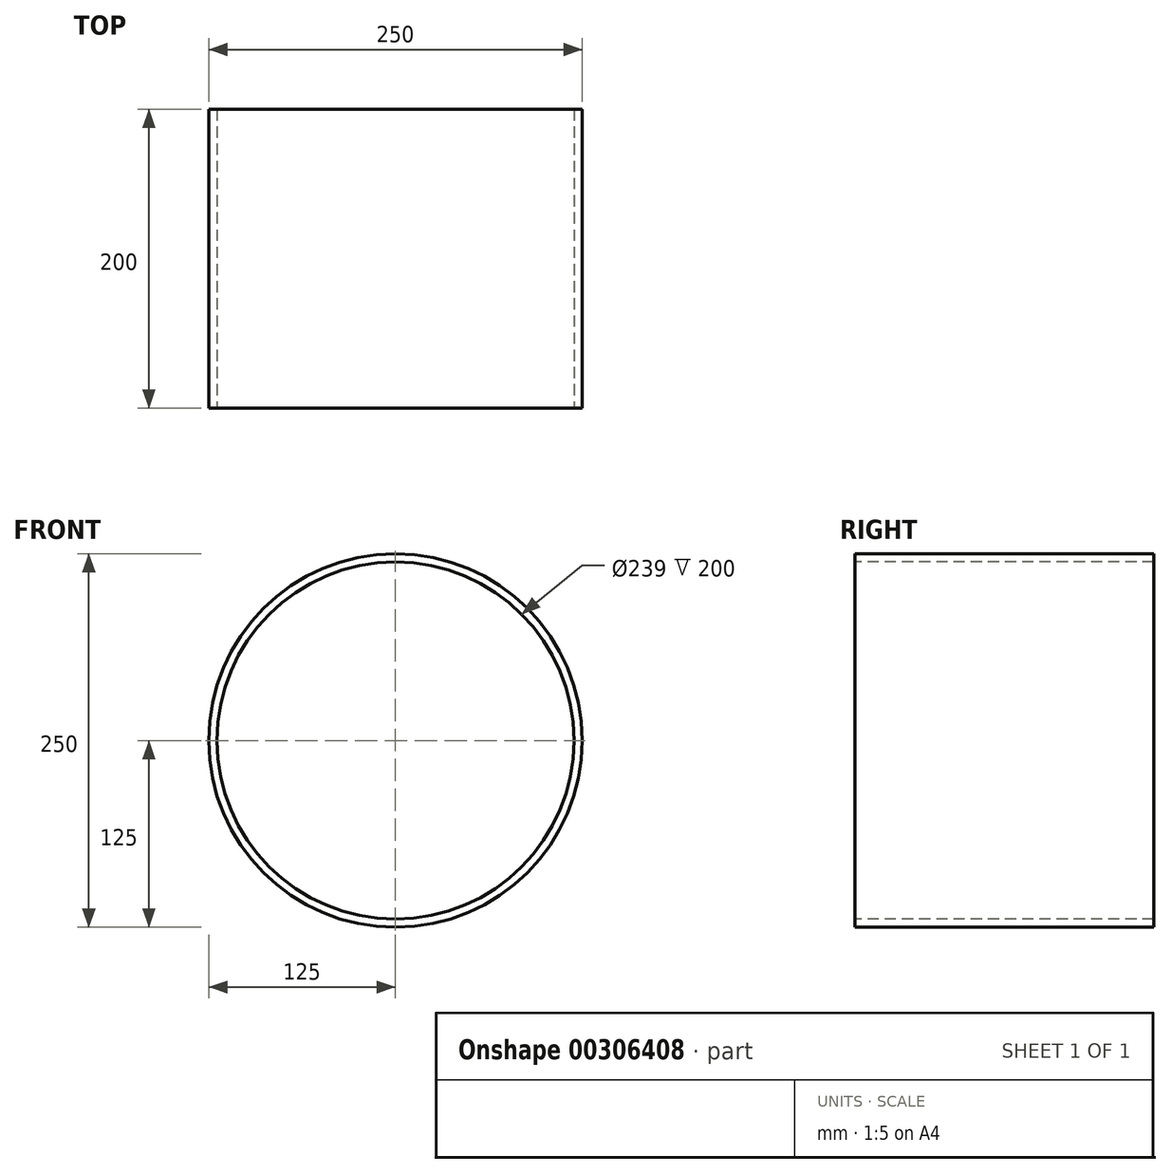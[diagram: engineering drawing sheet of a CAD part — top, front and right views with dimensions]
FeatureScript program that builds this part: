
annotation { "Feature Type Name" : "Feature", "Feature Type Description" : "" }
export const myFeature = defineFeature(function(context is Context, id is Id, definition is map)
    precondition{}
    {
        {
            var Q0;
            Q0=qCreatedBy(makeId("Front.planeOp"),FACE);
            var sketch = newSketch(context, id + "F0", { "sketchPlane" : qUnion([Q0])});
            skCircle(sketch, "E0", {"center": v(0, 0) * mm, "radius": 125 * mm});
            skCircle(sketch, "E1.0", {"center": v(0, 0) * mm, "radius": 119.5 * mm});
            skSolve(sketch);
        }
        {
            var Q0;
            Q0 = qSketchRegion(id + "F0", true);
            extrude(context, id + "F1", {"entities" : qUnion([Q0]), "oppositeDirection" : true, "depth" : 200 * mm});
        }
    });
